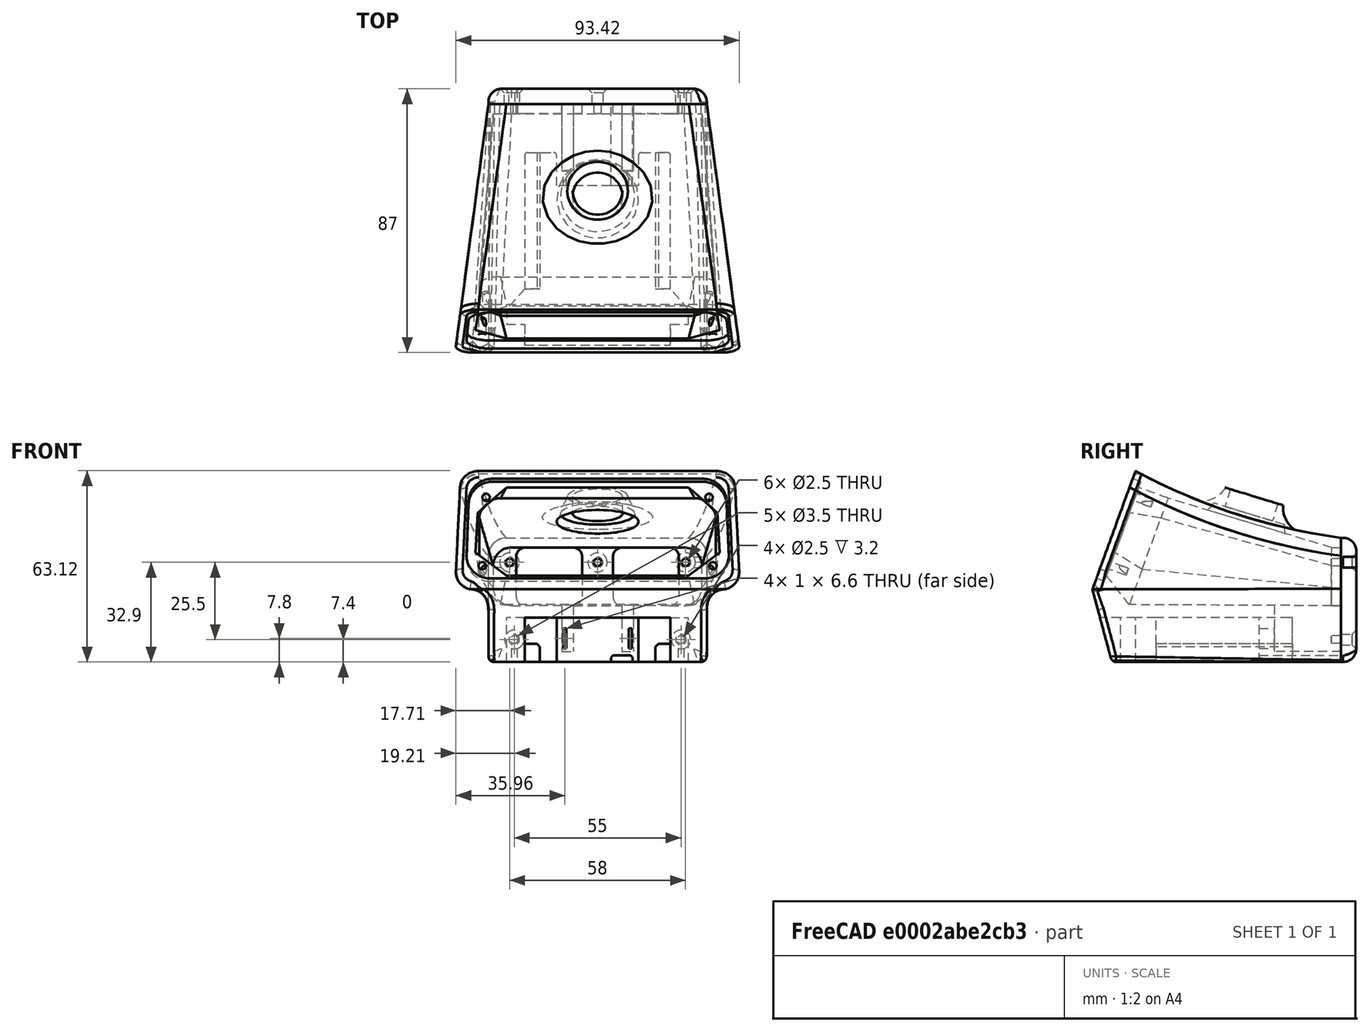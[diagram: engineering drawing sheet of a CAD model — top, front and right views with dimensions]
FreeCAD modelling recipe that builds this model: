
FCSTD DOCUMENT  (FreeCAD 0.19R24267 (Git))
Label: solder_station3
License: All rights reserved
LicenseURL: http://en.wikipedia.org/wiki/All_rights_reserved
objects: Sketcher::SketchObject×17, PartDesign::Pocket×7, Mesh::Feature×3, PartDesign::Pad×3, PartDesign::SubtractiveLoft×2, PartDesign::Fillet×2, PartDesign::Body×2, Spreadsheet::Sheet×1, PartDesign::Revolution×1, PartDesign::Groove×1, PartDesign::Chamfer×1, App::Part×1, Part::Fillet×1, App::DocumentObjectGroup×1
note: 54 computed .brp shape members not serialized (recipe doc carries the construction recipe); baked Part::Feature solids carry a one-line shape summary decoded from their .brp

FEATURE [Sketcher::SketchObject] Sketch  label="RearSupport"
  AttachmentOffset = pos=(0,0,-37.8) rot=(0,0,1;0rad)
  FullyConstrained = true
  MapMode = 5
  Placement = pos=(0,37.8,8.4e-15) rot=(1,0,0;1.5708rad)
  Support = -> [XZ_Plane004]
  expr: Constraints[51] = <<param>>.rear_screw_height
  expr: Constraints[50] = <<param>>.rear_screw_height
  expr: Constraints[49] = <<param>>.screw_hole
  expr: Constraints[52] = <<param>>.rear_screw_offset
  expr: Constraints[48] = <<param>>.rear_screw_width1
  expr: Constraints[47] = <<param>>.reart_screw_width2
  expr: Constraints[24] = 3
  expr: Constraints[39] = <<param>>.rear_height - <<param>>.wall
  expr: Constraints[38] = <<param>>.floor
  expr: Constraints[37] = <<param>>.bottom_height
  expr: .AttachmentOffset.Base.z = -<<param>>.mid_depth / 2 + <<param>>.wall
  sketch-geometry (22):
    g0: LineSegment StartX=-23.8 StartY=13.8 StartZ=0 EndX=-8.1 EndY=13.8 EndZ=0
    g1: LineSegment StartX=26.8 StartY=10.8 StartZ=0 EndX=26.8 EndY=-2.4 EndZ=0
    g2: LineSegment StartX=23.8 StartY=-5.4 StartZ=0 EndX=8.1 EndY=-5.4 EndZ=0
    g3: LineSegment StartX=-26.8 StartY=-2.4 StartZ=0 EndX=-26.8 EndY=10.8 EndZ=0
    g4: LineSegment StartX=-5.1 StartY=10.8 StartZ=0 EndX=-5.1 EndY=-2.4 EndZ=0
    g5: LineSegment StartX=5.1 StartY=10.8 StartZ=0 EndX=5.1 EndY=-2.4 EndZ=0
    g6: LineSegment StartX=8.1 StartY=13.8 StartZ=0 EndX=23.8 EndY=13.8 EndZ=0
    g7: LineSegment StartX=-8.1 StartY=-5.4 StartZ=0 EndX=-23.8 EndY=-5.4 EndZ=0
    g8: ArcOfCircle CenterX=-8.1 CenterY=10.8 CenterZ=0 NormalX=0 NormalY=0 NormalZ=1 AngleXU=0 Radius=3 StartAngle=0 EndAngle=1.5708
    g9: ArcOfCircle CenterX=8.1 CenterY=10.8 CenterZ=0 NormalX=0 NormalY=0 NormalZ=1 AngleXU=0 Radius=3 StartAngle=1.5708 EndAngle=3.14159
    g10: ArcOfCircle CenterX=-8.1 CenterY=-2.4 CenterZ=0 NormalX=0 NormalY=0 NormalZ=1 AngleXU=0 Radius=3 StartAngle=4.71239 EndAngle=6.28319
    g11: ArcOfCircle CenterX=8.1 CenterY=-2.4 CenterZ=0 NormalX=0 NormalY=0 NormalZ=1 AngleXU=0 Radius=3 StartAngle=3.14159 EndAngle=4.71239
    g12: ArcOfCircle CenterX=-23.8 CenterY=10.8 CenterZ=0 NormalX=0 NormalY=0 NormalZ=1 AngleXU=0 Radius=3 StartAngle=1.5708 EndAngle=3.14159
    g13: ArcOfCircle CenterX=-23.8 CenterY=-2.4 CenterZ=0 NormalX=0 NormalY=0 NormalZ=1 AngleXU=0 Radius=3 StartAngle=3.14159 EndAngle=4.71239
    g14: ArcOfCircle CenterX=23.8 CenterY=10.8 CenterZ=0 NormalX=0 NormalY=0 NormalZ=1 AngleXU=0 Radius=3 StartAngle=0 EndAngle=1.5708
    g15: ArcOfCircle CenterX=23.8 CenterY=-2.4 CenterZ=0 NormalX=0 NormalY=0 NormalZ=1 AngleXU=0 Radius=3 StartAngle=4.71239 EndAngle=6.28319
    g16: Circle CenterX=0 CenterY=-24 CenterZ=0 NormalX=0 NormalY=0 NormalZ=1 AngleXU=0 Radius=3
    g17: Circle CenterX=0 CenterY=8.9 CenterZ=0 NormalX=0 NormalY=0 NormalZ=1 AngleXU=0 Radius=1.25
    g18: Circle CenterX=-29 CenterY=8.9 CenterZ=0 NormalX=0 NormalY=0 NormalZ=1 AngleXU=0 Radius=1.25
    g19: Circle CenterX=-27.5 CenterY=-16.6 CenterZ=0 NormalX=0 NormalY=0 NormalZ=1 AngleXU=0 Radius=1.25
    g20: Circle CenterX=27.5 CenterY=-16.6 CenterZ=0 NormalX=0 NormalY=0 NormalZ=1 AngleXU=0 Radius=1.25
    g21: Circle CenterX=29 CenterY=8.9 CenterZ=0 NormalX=0 NormalY=0 NormalZ=1 AngleXU=0 Radius=1.25
  constraints (53):
    c: Horizontal(g0)
    c: Horizontal(g2)
    c: Vertical(g1)
    c: Vertical(g3)
    c: Vertical(g4)
    c: Vertical(g5)
    c: Tangent(g0,g6)
    c: Tangent(g2,g7)
    c: Tangent(g0,g8) = 1.5708
    c: Tangent(g4,g8) = 1.5708
    c: Tangent(g5,g9) = -1.5708
    c: Tangent(g6,g9) = 1.5708
    c: Tangent(g7,g10) = 1.5708
    c: Tangent(g4,g10) = 1.5708
    c: Tangent(g5,g11) = -1.5708
    c: Tangent(g2,g11) = 1.5708
    c: Tangent(g0,g12) = 1.5708
    c: Tangent(g3,g12) = 1.5708
    c: Tangent(g3,g13) = 1.5708
    c: Tangent(g7,g13) = 1.5708
    c: Tangent(g6,g14) = 1.5708
    c: Tangent(g1,g14) = 1.5708
    c: Tangent(g1,g15) = 1.5708
    c: Tangent(g2,g15) = 1.5708
    c: Radius(g9) = 3
    c: Equal(g12,g13)
    c: Equal(g13,g10)
    c: Equal(g10,g8)
    c: Equal(g11,g15)
    c: Equal(g15,g14)
    c: Equal(g14,g9)
    c: DistanceX(g4,g-1) = 5.1
    c: DistanceX(g5,g1) = 21.7
    c: Symmetric(g4,g5,g-2)
    c: Equal(g7,g2)
    c: PointOnObject(g16,g-2)
    c: Radius(g16) = 3
    c: DistanceY(g16,g-1) = 24
    c: DistanceY(g16,g2) = 18.6
    c: DistanceY(g16,g6) = 37.8
    c: PointOnObject(g17,g-2)
    c: Equal(g21,g18)
    c: Equal(g18,g19)
    c: Equal(g19,g20)
    c: Equal(g18,g17)
    c: Symmetric(g20,g19,g-2)
    c: Symmetric(g18,g21,g-2)
    c: DistanceX(g19,g20) = 55
    c: DistanceX(g18,g21) = 58
    c: Diameter(g19) = 2.5
    c: DistanceY(g20,g21) = 25.5
    c: DistanceY(g20,g17) = 25.5
    c: DistanceY(g16,g19) = 7.4
FEATURE [Spreadsheet::Sheet] Spreadsheet  label="param"
  cells = A1=Body; B2=top_depth; C2(top_depth)=70; B3=mid_depth; C3(mid_depth)=82; D3=half is rear reference; B4=bottom_depth; C4(bottom_depth)=75; B6=bottom_width; C6(bottom_width)=72; B7=bottom_height; C7(bottom_height)=24; B8=bottom_angle; C8(bottom_angle)=15; B10=rear_width; C10(rear_width)=72; B11=rear_height; C11(rear_height)=41; B13=mid_width; C13(mid_width)=80; B14=mid_height; C14(mid_height)=50; B16=front_width1; C16(front_width1)=91; D16=@top; E16=upper; B17=front_width2; C17(front_width2)=94; D17=@mid; E17=lower; B18=front_height; C18(front_height)=63; B19=front_angle; C19(front_angle)=20; B21=wall; C21(wall)=3.2; B22=radius_big; C22(radius_big)=6; B23=radius_small; C23(radius_small)=2; B24=arch; C24(arch)=200; A26=Button; B27=button_offset; C27(button_offset)=10; B28=button_inside_dia; C28(button_inside_dia)=20; B29=button_outside_dia; C29(button_outside_dia)=50; B30=button_height; C30(button_height)=23; B31=button_extension; C31(button_extension)=8; B32=button_fillet; C32(button_fillet)=12; B33=button_angle; C33(button_angle)=-17; B34=button_hole; C34(button_hole)=16.4; B35=button_hole_center; C35(button_hole_center)=-0.5; A37=Battery Cuts; B38=batt_carveout; C38(batt_carveout)=14.6; B39=batt_rail; C39(batt_rail)=6; B40=batt_rail_length; C40(batt_rail_length)=45; A42=Terminals; B43=terminal_height; C43(terminal_height)=6.6; B44=terminal_thickness; C44(terminal_thickness)=1; B45=terminal_seperation; C45(terminal_seperation)=21.5; B46=terminal_offset; C46(terminal_offset)=4.5; B47=terminal_depth; C47(terminal_depth)=22; A49=Box Interior; B50=floor; C50(floor)=18.6; B51=rear_inside_width; C51(rear_inside_width)==C10 - C21; D51=calc; B52=rear_inside_height; C52(rear_inside_height)==C11 - C21; D52=calc; B53=mid_inside_width; C53(mid_inside_width)==C13; D53=calc; B54=mid_inside_height; C54(mid_inside_height)==C14 + 6; D54=calc; B55=front_inside_width1; C55(front_inside_width1)==C62 - C58 * 2; D55=calc; E55=upper; B56=front_inside_width2; C56(front_inside_width2)==C63 - C58 * 2; D56=calc; E56=lower; B57=front_inside_height; C57(front_inside_height)==C64 - C59 * 2; D57=calc; B58=front_width_lip_width; C58(front_width_lip_width)=3; B59=front_inside_lip_height; C59(front_inside_lip_height)=2; A61=Face; B62=face_width1; C62(face_width1)==84 + 1; B63=face_width2; C63(face_width2)==85.5 + 1; B64=face_height; C64(face_height)==34 + 1; B65=face_thickness; C65(face_thickness)=3; B66=face_radius; C66(face_radius)=8; B67=face_offset; C67(face_offset)=2.8; D67=2.8; A69=Screws; B70=screw_hole; C70(screw_hole)=2.5; B72=front_screw_width1; C72(front_screw_width1)=73.5; D72=upper; B73=front_screw_width2; C73(front_screw_width2)=76; D73=lower; B74=front_screw_height; C74(front_screw_height)=24; B75=front_screw_offset; C75(front_screw_offset)=5.5; B77=rear_screw_width1; C77(rear_screw_width1)=58; B78=reart_screw_width2; C78(reart_screw_width2)=55; B79=rear_screw_height; C79(rear_screw_height)=25.5; B80=rear_screw_offset; C80(rear_screw_offset)=7.4
FEATURE [Sketcher::SketchObject] Sketch008  label="SketchButtonHole"
  AttachmentOffset = pos=(0,-0.5,23) rot=(1,0,0;-0.296706rad)
  FullyConstrained = true
  MapMode = 5
  Placement = pos=(0,-0.5,23) rot=(1,0,0;5.98648rad)
  Support = -> [XY_Plane004]
  expr: Constraints[2] = <<param>>.button_offset
  expr: .AttachmentOffset.Rotation.Angle = <<param>>.button_angle
  expr: .AttachmentOffset.Base.y = <<param>>.button_hole_center
  expr: Constraints[0] = <<param>>.button_hole
  expr: .AttachmentOffset.Base.z = <<param>>.button_height
  sketch-geometry (1):
    g0: Circle CenterX=0 CenterY=10 CenterZ=0 NormalX=0 NormalY=0 NormalZ=1 AngleXU=0 Radius=8.2
  constraints (3):
    c: Diameter(g0) = 16.4
    c: PointOnObject(g0,g-2)
    c: DistanceY(g-1,g0) = 10
FEATURE [Mesh::Feature] M18_soldering_case
  Placement = pos=(48,-41,-24) rot=(0,0.707107,0.707107;3.14159rad)
FEATURE [Sketcher::SketchObject] Sketch012  label="SketchSide"
  FullyConstrained = true
  MapMode = 5
  Placement = pos=(0,0,0) rot=(0.57735,0.57735,0.57735;2.0944rad)
  Support = -> [YZ_Plane004]
  expr: Constraints[21] = <<param>>.front_height
  expr: Constraints[6] = <<param>>.mid_depth
  expr: Constraints[17] = 90 - <<param>>.front_angle
  expr: Constraints[14] = <<param>>.bottom_height
  expr: Constraints[4] = <<param>>.rear_height - <<param>>.bottom_height
  expr: Constraints[5] = <<param>>.arch
  expr: Constraints[15] = <<param>>.radius_small
  expr: Constraints[16] = 90 - <<param>>.bottom_angle
  sketch-geometry (7):
    g0: LineSegment StartX=41 StartY=0 StartZ=0 EndX=41 EndY=17 EndZ=0
    g1: LineSegment StartX=-41 StartY=0 StartZ=0 EndX=-26.8052 EndY=39 EndZ=0
    g2: ArcOfCircle CenterX=67.8335 CenterY=215.192 CenterZ=0 NormalX=0 NormalY=0 NormalZ=1 AngleXU=0 Radius=200 StartAngle=4.21948 EndAngle=4.57782
    g3: LineSegment StartX=-41 StartY=0 StartZ=0 EndX=-34.9664 EndY=-22.5176 EndZ=0
    g4: LineSegment StartX=-33.0346 StartY=-24 StartZ=0 EndX=41 EndY=-24 EndZ=0
    g5: LineSegment StartX=41 StartY=-24 StartZ=0 EndX=41 EndY=0 EndZ=0
    g6: ArcOfCircle CenterX=-33.0346 CenterY=-22 CenterZ=0 NormalX=0 NormalY=0 NormalZ=1 AngleXU=0 Radius=2 StartAngle=3.40339 EndAngle=4.71239
  constraints (22):
    c: PointOnObject(g1,g-1)
    c: Vertical(g0)
    c: Coincident(g2,g0)
    c: Symmetric(g1,g0,g-2)
    c: DistanceY(g0,g0) = 17
    c: Radius(g2) = 200
    c: DistanceX(g1,g0) = 82
    c: Horizontal(g4)
    c: Coincident(g5,g4)
    c: Vertical(g5)
    c: Coincident(g6,g3)
    c: Coincident(g6,g4)
    c: Tangent(g6,g4)
    c: Tangent(g6,g3)
    c: DistanceY(g4,g-1) = 24
    c: Radius(g6) = 2
    c: Angle(g3,g-1) = 1.309
    c: Angle(g-1,g1) = 1.22173
    c: Coincident(g3,g1)
    c: Coincident(g5,g0)
    c: Coincident(g2,g1)
    c: DistanceY(g4,g1) = 63
FEATURE [Sketcher::SketchObject] Sketch018  label="SketchBat1"
  AttachmentOffset = pos=(0,0,-24) rot=(0,0,1;0rad)
  FullyConstrained = true
  MapMode = 5
  Placement = pos=(0,0,-24) rot=(0,0,1;0rad)
  Support = -> [XY_Plane004]
  expr: Constraints[64] = <<param>>.mid_depth / 2
  expr: .AttachmentOffset.Base.z = -<<param>>.bottom_height
  expr: Constraints[63] = <<param>>.batt_rail_length
  sketch-geometry (21):
    g0: LineSegment StartX=-24 StartY=-41.7082 StartZ=0 EndX=24 EndY=-41.7082 EndZ=0
    g1: LineSegment StartX=24 StartY=-41.7082 StartZ=0 EndX=24 EndY=-31.7082 EndZ=0
    g2: LineSegment StartX=24 StartY=-31.7082 StartZ=0 EndX=30 EndY=-31.7082 EndZ=0
    g3: LineSegment StartX=30 StartY=-31.7082 StartZ=0 EndX=30 EndY=-26.7082 EndZ=0
    g4: LineSegment StartX=30 StartY=-26.7082 StartZ=0 EndX=24 EndY=-20 EndZ=0
    g5: LineSegment StartX=24 StartY=-20 StartZ=0 EndX=24 EndY=24 EndZ=0
    g6: LineSegment StartX=13.5 StartY=24 StartZ=0 EndX=13.5 EndY=14 EndZ=0
    g7: LineSegment StartX=13.5 StartY=14 StartZ=0 EndX=-13.5 EndY=14 EndZ=0
    g8: LineSegment StartX=-13.5 StartY=14 StartZ=0 EndX=-13.5 EndY=24 EndZ=0
    g9: LineSegment StartX=-24 StartY=24 StartZ=0 EndX=-24 EndY=-20 EndZ=0
    g10: LineSegment StartX=-24 StartY=-20 StartZ=0 EndX=-30 EndY=-26.7082 EndZ=0
    g11: LineSegment StartX=-30 StartY=-26.7082 StartZ=0 EndX=-30 EndY=-31.7082 EndZ=0
    g12: LineSegment StartX=-30 StartY=-31.7082 StartZ=0 EndX=-24 EndY=-31.7082 EndZ=0
    g13: LineSegment StartX=-24 StartY=-31.7082 StartZ=0 EndX=-24 EndY=-41.7082 EndZ=0
    g14: Circle CenterX=0 CenterY=41 CenterZ=0 NormalX=0 NormalY=0 NormalZ=1 AngleXU=0 Radius=4
    g15: ArcOfCircle CenterX=-14.5 CenterY=24 CenterZ=0 NormalX=0 NormalY=0 NormalZ=1 AngleXU=0 Radius=1 StartAngle=6.28318 EndAngle=7.85399
    g16: LineSegment StartX=-23 StartY=25 StartZ=0 EndX=-14.5 EndY=25 EndZ=0
    g17: LineSegment StartX=14.5 StartY=25 StartZ=0 EndX=23 EndY=25 EndZ=0
    g18: ArcOfCircle CenterX=-23 CenterY=24 CenterZ=0 NormalX=0 NormalY=0 NormalZ=1 AngleXU=0 Radius=1 StartAngle=1.5708 EndAngle=3.1416
    g19: ArcOfCircle CenterX=14.5 CenterY=24 CenterZ=0 NormalX=0 NormalY=0 NormalZ=1 AngleXU=0 Radius=1 StartAngle=1.5708 EndAngle=3.14159
    g20: ArcOfCircle CenterX=23 CenterY=24 CenterZ=0 NormalX=0 NormalY=0 NormalZ=1 AngleXU=0 Radius=1.00001 StartAngle=2.74851e-06 EndAngle=1.5708
  constraints (65):
    c: Horizontal(g0)
    c: Coincident(g1,g0)
    c: Vertical(g1)
    c: Coincident(g2,g1)
    c: Horizontal(g2)
    c: Coincident(g3,g2)
    c: Coincident(g3,g4)
    c: Vertical(g5)
    c: Coincident(g6,g7)
    c: Coincident(g7,g8)
    c: Vertical(g8)
    c: Vertical(g9)
    c: Coincident(g10,g11)
    c: Vertical(g11)
    c: Coincident(g11,g12)
    c: Horizontal(g12)
    c: Coincident(g12,g13)
    c: Equal(g6,g8)
    c: Equal(g5,g9)
    c: Equal(g4,g10)
    c: Equal(g3,g11)
    c: Equal(g12,g2)
    c: Equal(g1,g13)
    c: Coincident(g13,g0)
    c: Vertical(g13)
    c: DistanceX(g7,g7) = 27
    c: Symmetric(g7,g6,g-2)
    c: Distance(g4) = 9
    c: Vertical(g3)
    c: DistanceY(g3,g3) = 5
    c: DistanceX(g2,g2) = 6
    c: DistanceY(g1,g1) = 10
    c: DistanceX(g0,g0) = 48
    c: PointOnObject(g14,g-2)
    c: Coincident(g9,g10)
    c: Coincident(g5,g4)
    c: Coincident(g15,g8)
    c: Coincident(g16,g15)
    c: Tangent(g15,g8)
    c: Horizontal(g16)
    c: Horizontal(g17)
    c: DistanceX(g9,g5) = 48
    c: Symmetric(g4,g9,g-2)
    c: Equal(g16,g17)
    c: Coincident(g18,g9)
    c: Coincident(g18,g16)
    c: Equal(g18,g15)
    c: Tangent(g18,g16)
    c: Tangent(g18,g9)
    c: DistanceY(g6,g17) = 11
    c: Vertical(g6)
    c: Coincident(g19,g6)
    c: Coincident(g19,g17)
    c: Coincident(g20,g17)
    c: Coincident(g20,g5)
    c: Tangent(g20,g17)
    c: Tangent(g20,g5)
    c: Tangent(g19,g6)
    c: Tangent(g19,g17)
    c: Equal(g15,g19)
    c: Radius(g19) = 1
    c: Radius(g14) = 4
    c: DistanceY(g15,g14) = 16
    c: DistanceY(g9,g16) = 45
    c: DistanceY(g-1,g14) = 41
FEATURE [Sketcher::SketchObject] Sketch019  label="SketchBat2"
  AttachmentOffset = pos=(0,0,-25) rot=(0,0,1;0rad)
  FullyConstrained = true
  MapMode = 5
  Placement = pos=(0,25,5.6e-15) rot=(1,0,0;1.5708rad)
  Support = -> [XZ_Plane004]
  expr: Constraints[18] = <<param>>.batt_rail
  expr: Constraints[17] = <<param>>.bottom_height
  expr: .AttachmentOffset.Base.z = -<<param>>.mid_depth / 2 + 16
  expr: Constraints[19] = 48.01mm
  sketch-geometry (10):
    g0: LineSegment StartX=-24.005 StartY=-18 StartZ=0 EndX=-20.005 EndY=-18 EndZ=0
    g1: LineSegment StartX=-19.005 StartY=-24 StartZ=0 EndX=-24.005 EndY=-24 EndZ=0
    g2: LineSegment StartX=-24.005 StartY=-24 StartZ=0 EndX=-24.005 EndY=-18 EndZ=0
    g3: LineSegment StartX=24.005 StartY=-18 StartZ=0 EndX=20.005 EndY=-18 EndZ=0
    g4: LineSegment StartX=19.005 StartY=-24 StartZ=0 EndX=24.005 EndY=-24 EndZ=0
    g5: LineSegment StartX=24.005 StartY=-24 StartZ=0 EndX=24.005 EndY=-18 EndZ=0
    g6: LineSegment StartX=-19.005 StartY=-19 StartZ=0 EndX=-19.005 EndY=-24 EndZ=0
    g7: LineSegment StartX=19.005 StartY=-24 StartZ=0 EndX=19.005 EndY=-19 EndZ=0
    g8: LineSegment StartX=-20.005 StartY=-18 StartZ=0 EndX=-19.005 EndY=-19 EndZ=0
    g9: LineSegment StartX=19.005 StartY=-19 StartZ=0 EndX=20.005 EndY=-18 EndZ=0
  constraints (29):
    c: Coincident(g1,g2)
    c: Coincident(g2,g0)
    c: Horizontal(g0)
    c: Horizontal(g1)
    c: Vertical(g2)
    c: Coincident(g4,g5)
    c: Coincident(g5,g3)
    c: Horizontal(g3)
    c: Horizontal(g4)
    c: Vertical(g5)
    c: Coincident(g6,g1)
    c: Vertical(g6)
    c: Equal(g1,g4)
    c: Coincident(g7,g4)
    c: Vertical(g7)
    c: Equal(g6,g7)
    c: Symmetric(g1,g4,g-2)
    c: DistanceY(g1,g-1) = 24
    c: DistanceY(g4,g3) = 6
    c: DistanceX(g1,g4) = 48.01
    c: DistanceX(g4,g4) = 5
    c: Coincident(g8,g0)
    c: Coincident(g8,g6)
    c: Coincident(g9,g7)
    c: Coincident(g9,g3)
    c: Equal(g0,g3)
    c: Equal(g2,g5)
    c: DistanceX(g0,g0) = 4
    c: DistanceY(g1,g6) = 5
FEATURE [Sketcher::SketchObject] Sketch021  label="SketchButton"
  AttachmentOffset = pos=(10,23,0) rot=(0,0,1;-0.296706rad)
  FullyConstrained = false
  MapMode = 5
  Placement = pos=(-2.9e-15,10,23) rot=(-0.51122,-0.690875,-0.51122;4.35074rad)
  Support = -> [YZ_Plane004]
  expr: Constraints[6] = <<param>>.button_extension
  expr: Constraints[7] = <<param>>.button_inside_dia / 2
  expr: Constraints[8] = <<param>>.button_outside_dia / 2
  expr: .AttachmentOffset.Base.y = <<param>>.button_height
  expr: .AttachmentOffset.Rotation.Angle = <<param>>.button_angle
  expr: .AttachmentOffset.Base.x = <<param>>.button_offset
  sketch-geometry (9):
    g0: LineSegment StartX=0 StartY=0 StartZ=0 EndX=0 EndY=8 EndZ=0
    g1: LineSegment StartX=0 StartY=8 StartZ=0 EndX=10 EndY=8 EndZ=0
    g2: LineSegment StartX=0 StartY=0 StartZ=0 EndX=25 EndY=0 EndZ=0
    g3: Circle CenterX=10 CenterY=8 CenterZ=0 NormalX=0 NormalY=0 NormalZ=1 AngleXU=0 Radius=1
    g4: Circle CenterX=11.7708 CenterY=0 CenterZ=0 NormalX=0 NormalY=0 NormalZ=1 AngleXU=0 Radius=1
    g5: Circle CenterX=25 CenterY=0 CenterZ=0 NormalX=0 NormalY=0 NormalZ=1 AngleXU=0 Radius=1
    g6: BSplineCurve PolesCount=3 KnotsCount=2 Degree=2 IsPeriodic=0
    g7: GeomPoint X=10 Y=8 Z=0
    g8: GeomPoint X=25 Y=0 Z=0
  constraints (20):
    c: Coincident(g0,g-1)
    c: PointOnObject(g0,g-2)
    c: Coincident(g1,g0)
    c: Horizontal(g1)
    c: Coincident(g2,g0)
    c: Horizontal(g2)
    c: DistanceY(g0,g0) = 8
    c: DistanceX(g1,g1) = 10
    c: DistanceX(g2,g2) = 25
    c: Coincident(g6,g1)
    c: Weight(g3) = 1
    c: Equal(g3,g4)
    c: Equal(g3,g5)
    c: Coincident(g6,g2)
    c: InternalAlignment(g3,g6)
    c: InternalAlignment(g4,g6)
    c: InternalAlignment(g5,g6)
    c: InternalAlignment(g7,g6)
    c: InternalAlignment(g8,g6)
    c: PointOnObject(g4,g2)
FEATURE [Sketcher::SketchObject] Sketch022  label="SketchRearInside"
  AttachmentOffset = pos=(0,0,-37.8) rot=(0,0,1;0rad)
  FullyConstrained = true
  MapMode = 5
  Placement = pos=(0,37.8,8.4e-15) rot=(1,0,0;1.5708rad)
  Support = -> [XZ_Plane004]
  expr: Constraints[29] = <<param>>.floor
  expr: Constraints[26] = <<param>>.bottom_height
  expr: Constraints[27] = <<param>>.rear_inside_height
  expr: .AttachmentOffset.Base.z = -<<param>>.mid_depth / 2 + <<param>>.wall
  expr: Constraints[18] = <<param>>.rear_inside_width
  expr: Constraints[12] = <<param>>.radius_big
  sketch-geometry (9):
    g0: LineSegment StartX=-34.4 StartY=7.80002 StartZ=0 EndX=-34.4 EndY=0.600003 EndZ=0
    g1: LineSegment StartX=-28.4 StartY=-5.4 StartZ=0 EndX=28.4 EndY=-5.4 EndZ=0
    g2: LineSegment StartX=34.4 StartY=0.600003 StartZ=0 EndX=34.4 EndY=7.80002 EndZ=0
    g3: LineSegment StartX=-28.4 StartY=13.8 StartZ=0 EndX=28.4 EndY=13.8 EndZ=0
    g4: ArcOfCircle CenterX=28.4 CenterY=7.8 CenterZ=0 NormalX=0 NormalY=0 NormalZ=1 AngleXU=0 Radius=6 StartAngle=3.92565e-06 EndAngle=1.5708
    g5: ArcOfCircle CenterX=28.4 CenterY=0.6 CenterZ=0 NormalX=0 NormalY=0 NormalZ=1 AngleXU=0 Radius=6 StartAngle=4.71239 EndAngle=6.28319
    g6: ArcOfCircle CenterX=-28.4 CenterY=7.8 CenterZ=0 NormalX=0 NormalY=0 NormalZ=1 AngleXU=0 Radius=6 StartAngle=1.5708 EndAngle=3.14159
    g7: ArcOfCircle CenterX=-28.4 CenterY=0.6 CenterZ=0 NormalX=0 NormalY=0 NormalZ=1 AngleXU=0 Radius=6 StartAngle=3.14159 EndAngle=4.71239
    g8: Circle CenterX=0 CenterY=-24 CenterZ=0 NormalX=0 NormalY=0 NormalZ=1 AngleXU=0 Radius=3
  constraints (30):
    c: Vertical(g0)
    c: Horizontal(g1)
    c: Vertical(g2)
    c: Horizontal(g3)
    c: Equal(g3,g1)
    c: Equal(g0,g2)
    c: Coincident(g4,g3)
    c: Coincident(g4,g2)
    c: Coincident(g5,g2)
    c: Coincident(g5,g1)
    c: Coincident(g6,g0)
    c: Coincident(g6,g3)
    c: Radius(g6) = 6
    c: Equal(g6,g4)
    c: Equal(g4,g5)
    c: Coincident(g7,g1)
    c: Coincident(g7,g0)
    c: Equal(g5,g7)
    c: DistanceX(g0,g2) = 68.8
    c: Symmetric(g0,g2,g-2)
    c: Tangent(g4,g2)
    c: Tangent(g4,g3)
    c: Tangent(g5,g2)
    c: Tangent(g5,g1)
    c: Tangent(g6,g3)
    c: PointOnObject(g8,g-2)
    c: DistanceY(g8,g-1) = 24
    c: DistanceY(g8,g3) = 37.8
    c: Radius(g8) = 3
    c: DistanceY(g8,g1) = 18.6
FEATURE [Sketcher::SketchObject] Sketch023  label="SketchFrontInside"
  AttachmentOffset = pos=(0,0,38) rot=(1,0,0;-0.349066rad)
  FullyConstrained = true
  MapMode = 5
  Placement = pos=(0,-38,-8.4e-15) rot=(-1,0,0;5.06145rad)
  Support = -> [XZ_Plane004]
  expr: Constraints[19] = <<param>>.front_inside_width2
  expr: Constraints[20] = <<param>>.front_inside_width2 / 2
  expr: Constraints[21] = <<param>>.face_offset + <<param>>.front_inside_lip_height
  expr: .AttachmentOffset.Rotation.Angle = -<<param>>.front_angle
  expr: Constraints[2] = <<param>>.front_inside_height
  expr: .AttachmentOffset.Base.z = <<param>>.mid_depth / 2 - <<param>>.face_thickness
  expr: Constraints[1] = <<param>>.front_inside_width1
  sketch-geometry (8):
    g0: LineSegment StartX=-30 StartY=4.8 StartZ=0 EndX=30 EndY=4.8 EndZ=0
    g1: LineSegment StartX=30 StartY=35.8 StartZ=0 EndX=-30 EndY=35.8 EndZ=0
    g2: LineSegment StartX=-39.5 StartY=26.8643 StartZ=0 EndX=-40.25 EndY=12.8643 EndZ=0
    g3: LineSegment StartX=-39.5 StartY=26.8643 StartZ=0 EndX=-30 EndY=35.8 EndZ=0
    g4: LineSegment StartX=30 StartY=35.8 StartZ=0 EndX=39.5 EndY=26.8643 EndZ=0
    g5: LineSegment StartX=40.25 StartY=12.8643 StartZ=0 EndX=30 EndY=4.8 EndZ=0
    g6: LineSegment StartX=-40.25 StartY=12.8643 StartZ=0 EndX=-30 EndY=4.8 EndZ=0
    g7: LineSegment StartX=39.5 StartY=26.8643 StartZ=0 EndX=40.25 EndY=12.8643 EndZ=0
  constraints (22):
    c: Symmetric(g0,g0,g-2)
    c: DistanceX(g2,g4) = 79
    c: DistanceY(g0,g1) = 31
    c: Symmetric(g1,g1,g-2)
    c: Coincident(g3,g2)
    c: Coincident(g3,g1)
    c: Coincident(g4,g1)
    c: Coincident(g5,g0)
    c: Coincident(g6,g2)
    c: Coincident(g6,g0)
    c: Equal(g3,g6)
    c: Equal(g6,g5)
    c: Equal(g5,g4)
    c: Coincident(g7,g4)
    c: Coincident(g7,g5)
    c: DistanceY(g7,g7) = 14
    c: Equal(g7,g2)
    c: Equal(g1,g0)
    c: DistanceX(g1,g1) = 60
    c: DistanceX(g2,g5) = 80.5
    c: DistanceX(g2,g-1) = 40.25
    c: DistanceY(g-1,g0) = 4.8
FEATURE [Sketcher::SketchObject] Sketch024  label="SketchFace"
  AttachmentOffset = pos=(0,0,38) rot=(1,0,0;-0.349066rad)
  FullyConstrained = true
  MapMode = 5
  Placement = pos=(0,-38,-8.4e-15) rot=(-1,0,0;5.06145rad)
  Support = -> [XZ_Plane004]
  expr: Constraints[25] = <<param>>.face_height
  expr: Constraints[24] = <<param>>.face_offset
  expr: .AttachmentOffset.Rotation.Angle = -<<param>>.front_angle
  expr: Constraints[22] = <<param>>.face_width1
  expr: Constraints[13] = <<param>>.face_radius
  expr: .AttachmentOffset.Base.z = <<param>>.mid_depth / 2 - <<param>>.face_thickness
  expr: Constraints[23] = <<param>>.face_width2
  sketch-geometry (8):
    g0: LineSegment StartX=-34.5062 StartY=37.8 StartZ=0 EndX=34.5063 EndY=37.8 EndZ=0
    g1: LineSegment StartX=42.5001 StartY=30.1155 StartZ=0 EndX=43.25 EndY=11.1155 EndZ=0
    g2: LineSegment StartX=35.2562 StartY=2.8 StartZ=0 EndX=-35.2562 EndY=2.8 EndZ=0
    g3: LineSegment StartX=-43.25 StartY=11.1156 StartZ=0 EndX=-42.4999 EndY=30.1156 EndZ=0
    g4: ArcOfCircle CenterX=34.5063 CenterY=29.8 CenterZ=0 NormalX=0 NormalY=0 NormalZ=1 AngleXU=0 Radius=8 StartAngle=0.0394514 EndAngle=1.5708
    g5: ArcOfCircle CenterX=35.2563 CenterY=10.8 CenterZ=0 NormalX=0 NormalY=0 NormalZ=1 AngleXU=0 Radius=8 StartAngle=4.71239 EndAngle=6.32264
    g6: ArcOfCircle CenterX=-34.5062 CenterY=29.8 CenterZ=0 NormalX=0 NormalY=0 NormalZ=1 AngleXU=0 Radius=8 StartAngle=1.5708 EndAngle=3.10214
    g7: ArcOfCircle CenterX=-35.2562 CenterY=10.8 CenterZ=0 NormalX=0 NormalY=0 NormalZ=1 AngleXU=0 Radius=8 StartAngle=3.10214 EndAngle=4.71239
  constraints (27):
    c: Horizontal(g0)
    c: Coincident(g4,g0)
    c: Coincident(g4,g1)
    c: Coincident(g5,g1)
    c: Coincident(g5,g2)
    c: Coincident(g6,g0)
    c: Coincident(g6,g3)
    c: Coincident(g7,g3)
    c: Coincident(g7,g2)
    c: Equal(g1,g3)
    c: Equal(g4,g6)
    c: Equal(g6,g7)
    c: Equal(g7,g5)
    c: Radius(g4) = 8
    c: Tangent(g6,g3)
    c: Tangent(g7,g3)
    c: Tangent(g7,g2)
    c: Tangent(g6,g0)
    c: Tangent(g4,g0)
    c: Tangent(g4,g1)
    c: Tangent(g5,g1)
    c: Tangent(g5,g2)
    c: DistanceX(g3,g1) = 85
    c: DistanceX(g3,g1) = 86.5
    c: DistanceY(g-1,g2) = 2.8
    c: DistanceY(g2,g0) = 35
    c: Symmetric(g2,g2,g-2)
FEATURE [Sketcher::SketchObject] Sketch025  label="SketchMidInside"
  AttachmentOffset = pos=(0,0,27) rot=(1,0,0;-0.349066rad)
  FullyConstrained = true
  MapMode = 5
  Placement = pos=(0,-27,-6e-15) rot=(-1,0,0;5.06145rad)
  Support = -> [XZ_Plane004]
  expr: Constraints[4] = <<param>>.bottom_height
  expr: Constraints[10] = <<param>>.radius_big + 1
  expr: Constraints[11] = <<param>>.floor
  expr: .AttachmentOffset.Base.z = <<param>>.mid_depth / 2 - 14
  expr: Constraints[12] = Spreadsheet.mid_inside_width - 2
  expr: Constraints[23] = <<param>>.mid_width - 16
  expr: .AttachmentOffset.Rotation.Angle = -<<param>>.front_angle
  expr: Constraints[14] = <<param>>.mid_inside_height
  sketch-geometry (9):
    g0: LineSegment StartX=-32 StartY=32 StartZ=0 EndX=32 EndY=32 EndZ=0
    g1: LineSegment StartX=39 StartY=25 StartZ=0 EndX=39 EndY=7 EndZ=0
    g2: LineSegment StartX=32 StartY=-5.4 StartZ=0 EndX=-32 EndY=-5.4 EndZ=0
    g3: LineSegment StartX=-39 StartY=7 StartZ=0 EndX=-39 EndY=25 EndZ=0
    g4: Circle CenterX=0 CenterY=-24 CenterZ=0 NormalX=0 NormalY=0 NormalZ=1 AngleXU=0 Radius=3
    g5: ArcOfCircle CenterX=-32 CenterY=25 CenterZ=0 NormalX=0 NormalY=0 NormalZ=1 AngleXU=0 Radius=7 StartAngle=1.5708 EndAngle=3.14159
    g6: ArcOfCircle CenterX=32 CenterY=25 CenterZ=0 NormalX=0 NormalY=0 NormalZ=1 AngleXU=0 Radius=7 StartAngle=0 EndAngle=1.5708
    g7: ArcOfCircle CenterX=-15.541 CenterY=12.0672 CenterZ=0 NormalX=0 NormalY=0 NormalZ=1 AngleXU=0 Radius=24 StartAngle=3.35433 EndAngle=3.9567
    g8: ArcOfCircle CenterX=15.541 CenterY=12.0672 CenterZ=0 NormalX=0 NormalY=0 NormalZ=1 AngleXU=0 Radius=24 StartAngle=5.46808 EndAngle=6.07045
  constraints (25):
    c: Vertical(g1)
    c: Vertical(g3)
    c: PointOnObject(g4,g-2)
    c: Radius(g4) = 3
    c: DistanceY(g4,g-1) = 24
    c: Tangent(g3,g5) = 1.5708
    c: Tangent(g0,g5) = 1.5708
    c: Tangent(g0,g6) = 1.5708
    c: Tangent(g1,g6) = 1.5708
    c: Equal(g6,g5)
    c: Radius(g6) = 7
    c: DistanceY(g4,g2) = 18.6
    c: DistanceX(g3,g1) = 78
    c: Symmetric(g2,g2,g-2)
    c: DistanceY(g4,g0) = 56
    c: Symmetric(g0,g0,g-2)
    c: Equal(g3,g1)
    c: Coincident(g7,g2)
    c: Coincident(g8,g1)
    c: Coincident(g8,g2)
    c: Coincident(g7,g3)
    c: Equal(g8,g7)
    c: Radius(g8) = 24
    c: DistanceX(g2,g2) = 64
    c: DistanceY(g1,g1) = 18
FEATURE [Sketcher::SketchObject] Sketch026  label="SketchFrontScrews"
  AttachmentOffset = pos=(0,0,38) rot=(1,0,0;-0.349066rad)
  FullyConstrained = true
  MapMode = 5
  Placement = pos=(0,-38,-8.4e-15) rot=(-1,0,0;5.06145rad)
  Support = -> [XZ_Plane004]
  expr: .AttachmentOffset.Rotation.Angle = -<<param>>.front_angle
  expr: Constraints[9] = <<param>>.face_offset + <<param>>.front_screw_offset
  expr: .AttachmentOffset.Base.z = <<param>>.mid_depth / 2 - <<param>>.face_thickness
  expr: Constraints[13] = <<param>>.screw_hole
  expr: Constraints[2] = <<param>>.front_screw_height
  expr: Constraints[1] = <<param>>.front_screw_width2
  expr: Constraints[0] = <<param>>.front_screw_width1
  sketch-geometry (6):
    g0: Circle CenterX=-36.75 CenterY=32.3 CenterZ=0 NormalX=0 NormalY=0 NormalZ=1 AngleXU=0 Radius=1.25
    g1: Circle CenterX=36.75 CenterY=32.3 CenterZ=0 NormalX=0 NormalY=0 NormalZ=1 AngleXU=0 Radius=1.25
    g2: Circle CenterX=-38 CenterY=8.3 CenterZ=0 NormalX=0 NormalY=0 NormalZ=1 AngleXU=0 Radius=1.25
    g3: Circle CenterX=38 CenterY=8.3 CenterZ=0 NormalX=0 NormalY=0 NormalZ=1 AngleXU=0 Radius=1.25
    g4: LineSegment StartX=-36.75 StartY=32.3 StartZ=0 EndX=36.75 EndY=32.3 EndZ=0
    g5: LineSegment StartX=-38 StartY=8.3 StartZ=0 EndX=38 EndY=8.3 EndZ=0
  constraints (14):
    c: DistanceX(g0,g1) = 73.5
    c: DistanceX(g2,g3) = 76
    c: DistanceY(g3,g1) = 24
    c: Coincident(g4,g0)
    c: Coincident(g4,g1)
    c: Coincident(g5,g2)
    c: Coincident(g5,g3)
    c: Symmetric(g2,g3,g-2)
    c: Symmetric(g0,g1,g-2)
    c: DistanceY(g-1,g3) = 8.3
    c: Equal(g0,g2)
    c: Equal(g2,g3)
    c: Equal(g3,g1)
    c: Diameter(g0) = 2.5
FEATURE [Sketcher::SketchObject] Sketch027  label="SketchButtonCarve"
  AttachmentOffset = pos=(10,23,0) rot=(0,0,1;-0.296706rad)
  FullyConstrained = true
  MapMode = 5
  Placement = pos=(-2.9e-15,10,23) rot=(-0.51122,-0.690875,-0.51122;4.35074rad)
  Support = -> [YZ_Plane004]
  expr: Constraints[12] = <<param>>.button_hole / 2 + 10
  expr: .AttachmentOffset.Base.x = <<param>>.button_offset
  expr: Constraints[6] = <<param>>.button_hole / 2 + 4
  expr: .AttachmentOffset.Base.y = <<param>>.button_height
  expr: .AttachmentOffset.Rotation.Angle = <<param>>.button_angle
  sketch-geometry (4):
    g0: LineSegment StartX=0 StartY=2 StartZ=0 EndX=12.2 EndY=2 EndZ=0
    g1: ArcOfCircle CenterX=18.2 CenterY=3.09999 CenterZ=0 NormalX=0 NormalY=0 NormalZ=1 AngleXU=0 Radius=6.09999 StartAngle=3.32291 EndAngle=4.71239
    g2: LineSegment StartX=0 StartY=2 StartZ=0 EndX=0 EndY=-3 EndZ=0
    g3: LineSegment StartX=18.2 StartY=-3 StartZ=0 EndX=0 EndY=-3 EndZ=0
  constraints (13):
    c: Horizontal(g0)
    c: Coincident(g1,g0)
    c: Coincident(g2,g0)
    c: Coincident(g3,g1)
    c: Horizontal(g3)
    c: Tangent(g3,g1)
    c: DistanceX(g0,g0) = 12.2
    c: DistanceY(g2,g2) = 5
    c: Coincident(g2,g3)
    c: Vertical(g2)
    c: PointOnObject(g-1,g2)
    c: DistanceY(g2,g-1) = 3
    c: DistanceX(g3,g3) = 18.2
FEATURE [Sketcher::SketchObject] Sketch028  label="SketchTerminals"
  FullyConstrained = true
  MapMode = 5
  Placement = pos=(0,0,0) rot=(1,0,0;1.5708rad)
  Support = -> [XZ_Plane004]
  expr: Constraints[24] = <<param>>.terminal_seperation
  expr: Constraints[23] = <<param>>.terminal_offset
  expr: Constraints[19] = <<param>>.terminal_height
  expr: Constraints[22] = <<param>>.bottom_height
  expr: Constraints[18] = <<param>>.terminal_thickness
  sketch-geometry (15):
    g0: LineSegment StartX=10.25 StartY=-12.9 StartZ=0 EndX=11.25 EndY=-12.9 EndZ=0
    g1: LineSegment StartX=11.25 StartY=-12.9 StartZ=0 EndX=11.25 EndY=-19.5 EndZ=0
    g2: LineSegment StartX=11.25 StartY=-19.5 StartZ=0 EndX=10.25 EndY=-19.5 EndZ=0
    g3: LineSegment StartX=10.25 StartY=-19.5 StartZ=0 EndX=10.25 EndY=-12.9 EndZ=0
    g4: LineSegment StartX=-10.25 StartY=-12.9 StartZ=0 EndX=-11.25 EndY=-12.9 EndZ=0
    g5: LineSegment StartX=-11.25 StartY=-12.9 StartZ=0 EndX=-11.25 EndY=-19.5 EndZ=0
    g6: LineSegment StartX=-11.25 StartY=-19.5 StartZ=0 EndX=-10.25 EndY=-19.5 EndZ=0
    g7: LineSegment StartX=-10.25 StartY=-19.5 StartZ=0 EndX=-10.25 EndY=-12.9 EndZ=0
    g8: Circle CenterX=0 CenterY=-24 CenterZ=0 NormalX=0 NormalY=0 NormalZ=1 AngleXU=0 Radius=3
    g9: LineSegment StartX=4.5 StartY=-24 StartZ=0 EndX=11.5 EndY=-24 EndZ=0
    g10: LineSegment StartX=11.5 StartY=-24 StartZ=0 EndX=11.5 EndY=-22.8 EndZ=0
    g11: LineSegment StartX=10.5 StartY=-21.8 StartZ=0 EndX=5.5 EndY=-21.8 EndZ=0
    g12: LineSegment StartX=4.5 StartY=-22.8 StartZ=0 EndX=4.5 EndY=-24 EndZ=0
    g13: ArcOfCircle CenterX=5.5 CenterY=-22.8 CenterZ=0 NormalX=0 NormalY=0 NormalZ=1 AngleXU=0 Radius=1 StartAngle=1.5708 EndAngle=3.14159
    g14: ArcOfCircle CenterX=10.5 CenterY=-22.8 CenterZ=0 NormalX=0 NormalY=0 NormalZ=1 AngleXU=0 Radius=1 StartAngle=7e-16 EndAngle=1.5708
  constraints (42):
    c: Coincident(g0,g1)
    c: Coincident(g1,g2)
    c: Coincident(g2,g3)
    c: Coincident(g3,g0)
    c: Horizontal(g0)
    c: Horizontal(g2)
    c: Vertical(g1)
    c: Vertical(g3)
    c: Coincident(g4,g5)
    c: Coincident(g5,g6)
    c: Coincident(g6,g7)
    c: Coincident(g7,g4)
    c: Horizontal(g4)
    c: Horizontal(g6)
    c: Vertical(g5)
    c: Vertical(g7)
    c: Equal(g7,g1)
    c: Equal(g4,g0)
    c: DistanceX(g4,g4) = 1
    c: DistanceY(g3,g3) = 6.6
    c: PointOnObject(g8,g-2)
    c: Radius(g8) = 3
    c: DistanceY(g8,g-1) = 24
    c: DistanceY(g8,g1) = 4.5
    c: DistanceX(g6,g1) = 21.5
    c: Symmetric(g4,g0,g-2)
    c: Coincident(g9,g10)
    c: Coincident(g12,g9)
    c: Horizontal(g9)
    c: Horizontal(g11)
    c: Vertical(g10)
    c: Vertical(g12)
    c: Tangent(g12,g13) = -1.5708
    c: Tangent(g11,g13) = -1.5708
    c: Tangent(g11,g14) = -1.5708
    c: Tangent(g10,g14) = -1.5708
    c: DistanceX(g9,g9) = 7
    c: DistanceY(g9,g11) = 2.2
    c: DistanceX(g8,g9) = 4.5
    c: Equal(g13,g14)
    c: Radius(g14) = 1
    c: DistanceY(g8,g9) = 0
FEATURE [Sketcher::SketchObject] Sketch029  label="SketchAccess"
  AttachmentOffset = pos=(0,0,-41) rot=(0,0,1;0rad)
  FullyConstrained = true
  MapMode = 5
  Placement = pos=(0,41,9.1e-15) rot=(1,0,0;1.5708rad)
  Support = -> [XZ_Plane004]
  expr: .AttachmentOffset.Base.z = -<<param>>.mid_depth / 2
  expr: Constraints[5] = <<param>>.bottom_height
  expr: Constraints[17] = <<param>>.terminal_seperation + <<param>>.terminal_thickness * 2
  expr: Constraints[25] = <<param>>.terminal_offset - 1
  sketch-geometry (9):
    g0: LineSegment StartX=-11.75 StartY=-0.5 StartZ=0 EndX=-11.75 EndY=-20.5 EndZ=0
    g1: LineSegment StartX=-7.95 StartY=-0.5 StartZ=0 EndX=-7.95 EndY=-20.5 EndZ=0
    g2: LineSegment StartX=7.95 StartY=-0.5 StartZ=0 EndX=7.95 EndY=-20.5 EndZ=0
    g3: LineSegment StartX=11.75 StartY=-0.5 StartZ=0 EndX=11.75 EndY=-20.5 EndZ=0
    g4: Circle CenterX=0 CenterY=-24 CenterZ=0 NormalX=0 NormalY=0 NormalZ=1 AngleXU=0 Radius=3
    g5: LineSegment StartX=-11.75 StartY=-20.5 StartZ=0 EndX=-7.95 EndY=-20.5 EndZ=0
    g6: LineSegment StartX=-11.75 StartY=-0.5 StartZ=0 EndX=-7.95 EndY=-0.5 EndZ=0
    g7: LineSegment StartX=7.95 StartY=-0.5 StartZ=0 EndX=11.75 EndY=-0.5 EndZ=0
    g8: LineSegment StartX=7.95 StartY=-20.5 StartZ=0 EndX=11.75 EndY=-20.5 EndZ=0
  constraints (26):
    c: Vertical(g0)
    c: Vertical(g2)
    c: Equal(g1,g2)
    c: PointOnObject(g4,g-2)
    c: Radius(g4) = 3
    c: DistanceY(g4,g-1) = 24
    c: Coincident(g5,g0)
    c: Coincident(g5,g1)
    c: Coincident(g6,g0)
    c: Coincident(g6,g1)
    c: Horizontal(g6)
    c: Coincident(g7,g2)
    c: Coincident(g7,g3)
    c: Horizontal(g7)
    c: Coincident(g8,g2)
    c: Coincident(g8,g3)
    c: Horizontal(g8)
    c: DistanceX(g0,g3) = 23.5
    c: Vertical(g3)
    c: Equal(g7,g6)
    c: DistanceY(g3,g3) = 20
    c: Symmetric(g1,g2,g-2)
    c: DistanceX(g6,g6) = 3.8
    c: Vertical(g1)
    c: Horizontal(g5)
    c: DistanceY(g4,g1) = 3.5
FEATURE [PartDesign::Pad] Pad  label="PadSide"
  Direction = (1,1,1)
  Length = 110
  Length2 = 100
  Midplane = true
  Placement = pos=(0,0,0) rot=(0.57735,0.57735,0.57735;2.0944rad)
  Profile = -> Sketch012
  Type = 0
FEATURE [Sketcher::SketchObject] Sketch030  label="SketchFront"
  AttachmentOffset = pos=(0,0,41) rot=(0,0,1;0rad)
  FullyConstrained = true
  MapMode = 5
  Placement = pos=(0,-41,-9.1e-15) rot=(1,0,0;1.5708rad)
  Support = -> [XZ_Plane004]
  expr: .AttachmentOffset.Base.z = <<param>>.mid_depth / 2
  expr: Constraints[13] = <<param>>.front_width2
  expr: Constraints[12] = <<param>>.bottom_height
  expr: Constraints[15] = <<param>>.front_height + 14
  expr: Constraints[29] = <<param>>.radius_big
  expr: Constraints[14] = <<param>>.front_width2
  expr: Constraints[9] = <<param>>.radius_small
  expr: Constraints[10] = <<param>>.bottom_width
  sketch-geometry (16):
    g0: LineSegment StartX=-47 StartY=53 StartZ=0 EndX=47 EndY=53 EndZ=0
    g1: LineSegment StartX=47 StartY=53 StartZ=0 EndX=47 EndY=5.97913 EndZ=0
    g2: LineSegment StartX=36 StartY=-5.97912 StartZ=0 EndX=36 EndY=-22 EndZ=0
    g3: LineSegment StartX=34 StartY=-24 StartZ=0 EndX=-34 EndY=-24 EndZ=0
    g4: LineSegment StartX=-36 StartY=-22 StartZ=0 EndX=-36 EndY=-5.97912 EndZ=0
    g5: LineSegment StartX=-47 StartY=5.97912 StartZ=0 EndX=-47 EndY=53 EndZ=0
    g6: ArcOfCircle CenterX=-34 CenterY=-22 CenterZ=0 NormalX=0 NormalY=0 NormalZ=1 AngleXU=0 Radius=2 StartAngle=3.14159 EndAngle=4.71239
    g7: ArcOfCircle CenterX=34 CenterY=-22 CenterZ=0 NormalX=0 NormalY=0 NormalZ=1 AngleXU=0 Radius=2 StartAngle=4.71239 EndAngle=6.28319
    g8: LineSegment StartX=-75 StartY=75 StartZ=0 EndX=75 EndY=75 EndZ=0
    g9: LineSegment StartX=75 StartY=75 StartZ=0 EndX=75 EndY=-75 EndZ=0
    g10: LineSegment StartX=75 StartY=-75 StartZ=0 EndX=-75 EndY=-75 EndZ=0
    g11: LineSegment StartX=-75 StartY=-75 StartZ=0 EndX=-75 EndY=75 EndZ=0
    g12: ArcOfCircle CenterX=42 CenterY=-5.97912 CenterZ=0 NormalX=0 NormalY=0 NormalZ=1 AngleXU=0 Radius=5.99999 StartAngle=1.65423 EndAngle=3.14159
    g13: ArcOfCircle CenterX=41 CenterY=5.97913 CenterZ=0 NormalX=0 NormalY=0 NormalZ=1 AngleXU=0 Radius=6 StartAngle=4.79582 EndAngle=6.28319
    g14: ArcOfCircle CenterX=-42 CenterY=-5.97912 CenterZ=0 NormalX=0 NormalY=0 NormalZ=1 AngleXU=0 Radius=5.99999 StartAngle=6.28319 EndAngle=7.77055
    g15: ArcOfCircle CenterX=-41 CenterY=5.97913 CenterZ=0 NormalX=0 NormalY=0 NormalZ=1 AngleXU=0 Radius=6 StartAngle=3.14159 EndAngle=4.62896
  constraints (42):
    c: Coincident(g0,g1)
    c: Vertical(g2)
    c: Vertical(g4)
    c: Coincident(g5,g0)
    c: Tangent(g4,g6) = 1.5708
    c: Tangent(g3,g6) = 1.5708
    c: Tangent(g3,g7) = 1.5708
    c: Tangent(g2,g7) = 1.5708
    c: Equal(g7,g6)
    c: Radius(g7) = 2
    c: DistanceX(g4,g2) = 72
    c: Symmetric(g3,g3,g-2)
    c: DistanceY(g3,g-1) = 24
    c: DistanceX(g5,g1) = 94
    c: DistanceX(g0,g0) = 94
    c: DistanceY(g3,g0) = 77
    c: Symmetric(g0,g0,g-2)
    c: Coincident(g8,g9)
    c: Coincident(g9,g10)
    c: Coincident(g10,g11)
    c: Coincident(g11,g8)
    c: Horizontal(g10)
    c: Vertical(g11)
    c: Symmetric(g8,g8,g-2)
    c: Symmetric(g8,g9,g-1)
    c: Equal(g8,g9)
    c: Coincident(g14,g4)
    c: Coincident(g15,g14)
    c: Coincident(g15,g5)
    c: Radius(g13) = 6
    c: DistanceX(g8,g8) = 150
    c: Vertical(g5)
    c: Tangent(g13,g12) = 1.5708
    c: Tangent(g13,g1) = 1.5708
    c: Tangent(g12,g2) = -1.5708
    c: Tangent(g14,g4)
    c: Tangent(g14,g15)
    c: Symmetric(g5,g4,g14)
    c: Equal(g14,g12)
    c: Equal(g13,g15)
    c: PointOnObject(g12,g-1)
    c: PointOnObject(g14,g-1)
FEATURE [Sketcher::SketchObject] Sketch031  label="SketchRear"
  AttachmentOffset = pos=(0,0,-41) rot=(0,0,1;0rad)
  FullyConstrained = true
  MapMode = 5
  Placement = pos=(0,41,9.1e-15) rot=(1,0,0;1.5708rad)
  Support = -> [XZ_Plane004]
  expr: Constraints[16] = <<param>>.rear_width
  expr: .AttachmentOffset.Base.z = -<<param>>.mid_depth / 2
  expr: Constraints[4] = <<param>>.front_height + 14
  expr: Constraints[1] = <<param>>.radius_small
  expr: Constraints[5] = <<param>>.bottom_height
  expr: Constraints[2] = <<param>>.rear_width
  sketch-geometry (10):
    g0: LineSegment StartX=-34 StartY=-24 StartZ=0 EndX=34 EndY=-24 EndZ=0
    g1: LineSegment StartX=36 StartY=53 StartZ=0 EndX=-36 EndY=53 EndZ=0
    g2: ArcOfCircle CenterX=-34 CenterY=-22 CenterZ=0 NormalX=0 NormalY=0 NormalZ=1 AngleXU=0 Radius=2 StartAngle=3.14159 EndAngle=4.71239
    g3: ArcOfCircle CenterX=34 CenterY=-22 CenterZ=0 NormalX=0 NormalY=0 NormalZ=1 AngleXU=0 Radius=2 StartAngle=4.71238 EndAngle=6.28319
    g4: LineSegment StartX=-75 StartY=75 StartZ=0 EndX=75 EndY=75 EndZ=0
    g5: LineSegment StartX=75 StartY=75 StartZ=0 EndX=75 EndY=-75 EndZ=0
    g6: LineSegment StartX=75 StartY=-75 StartZ=0 EndX=-75 EndY=-75 EndZ=0
    g7: LineSegment StartX=-75 StartY=-75 StartZ=0 EndX=-75 EndY=75 EndZ=0
    g8: LineSegment StartX=36 StartY=-22 StartZ=0 EndX=36 EndY=53 EndZ=0
    g9: LineSegment StartX=-36 StartY=-22 StartZ=0 EndX=-36 EndY=53 EndZ=0
  constraints (29):
    c: Horizontal(g0)
    c: Radius(g3) = 2
    c: DistanceX(g1,g1) = 72
    c: Symmetric(g1,g1,g-2)
    c: DistanceY(g0,g1) = 77
    c: DistanceY(g0,g-1) = 24
    c: Coincident(g4,g5)
    c: Coincident(g5,g6)
    c: Coincident(g6,g7)
    c: Coincident(g7,g4)
    c: Horizontal(g4)
    c: Vertical(g7)
    c: Symmetric(g5,g6,g-2)
    c: DistanceX(g4,g4) = 150
    c: Equal(g4,g5)
    c: Symmetric(g4,g5,g-1)
    c: DistanceX(g2,g3) = 72
    c: Coincident(g8,g3)
    c: Coincident(g8,g1)
    c: Vertical(g8)
    c: Coincident(g9,g2)
    c: Coincident(g9,g1)
    c: Equal(g9,g8)
    c: Horizontal(g3,g3)
    c: Horizontal(g2,g2)
    c: Equal(g2,g3)
    c: Coincident(g0,g2)
    c: Coincident(g0,g3)
    c: Vertical(g2,g0)
FEATURE [PartDesign::SubtractiveLoft] SubtractiveLoft001  label="SubtractiveLoftTaper"
  BaseFeature = -> Pad
  Closed = false
  Placement = pos=(0,0,0) rot=(0.57735,0.57735,0.57735;2.0944rad)
  Profile = -> Sketch031
  Ruled = true
  Sections = -> [Sketch030]
FEATURE [PartDesign::Pocket] Pocket  label="PocketBatt"
  BaseFeature = -> SubtractiveLoft001
  Length = 14.6
  Length2 = 100
  Placement = pos=(0,0,0) rot=(0.57735,0.57735,0.57735;2.0944rad)
  Profile = -> Sketch018
  Reversed = true
  Type = 0
  expr: Length = Spreadsheet.batt_carveout
FEATURE [PartDesign::Pad] Pad004  label="PadRail"
  BaseFeature = -> Pocket
  Direction = (1,1,1)
  Length = 45
  Length2 = 100
  Placement = pos=(0,0,0) rot=(0.57735,0.57735,0.57735;2.0944rad)
  Profile = -> Sketch019
  Type = 0
  expr: Length = <<param>>.batt_rail_length
FEATURE [PartDesign::Pocket] Pocket002  label="PocketRear"
  BaseFeature = -> Pad004
  Length = 6
  Length2 = 100
  Placement = pos=(0,0,0) rot=(0.57735,0.57735,0.57735;2.0944rad)
  Profile = -> Sketch
  Type = 0
FEATURE [PartDesign::SubtractiveLoft] SubtractiveLoft  label="SubtractiveLoftInside"
  BaseFeature = -> Pocket002
  Closed = false
  Placement = pos=(0,0,0) rot=(0.57735,0.57735,0.57735;2.0944rad)
  Profile = -> Sketch022
  Ruled = true
  Sections = -> [Sketch025,Sketch023]
FEATURE [PartDesign::Pocket] Pocket003  label="PocketFace"
  BaseFeature = -> SubtractiveLoft
  Length = 3.2
  Length2 = 100
  Placement = pos=(0,0,0) rot=(0.57735,0.57735,0.57735;2.0944rad)
  Profile = -> Sketch024
  Reversed = true
  Type = 0
  expr: Length = <<param>>.face_thickness + 0.2
FEATURE [PartDesign::Pocket] Pocket004  label="PocketFrontScrews"
  BaseFeature = -> Pocket003
  Length = 6
  Length2 = 100
  Placement = pos=(0,0,0) rot=(0.57735,0.57735,0.57735;2.0944rad)
  Profile = -> Sketch026
  Type = 0
FEATURE [PartDesign::Revolution] Revolution  label="RevolutionButton"
  Angle = 360
  Axis = (-1e-16,0.292372,0.956305)
  Base = (-2.9e-15,10,23)
  BaseFeature = -> Pocket004
  Placement = pos=(0,0,0) rot=(0.57735,0.57735,0.57735;2.0944rad)
  Profile = -> Sketch021
  ReferenceAxis = -> Sketch021 [V_Axis]
  Reversed = true
FEATURE [PartDesign::Pocket] Pocket005  label="PocketButtonHole"
  BaseFeature = -> Revolution
  Length = 6
  Length2 = 100
  Placement = pos=(0,0,0) rot=(0.57735,0.57735,0.57735;2.0944rad)
  Profile = -> Sketch008
  Reversed = true
  Type = 1
FEATURE [PartDesign::Groove] Groove  label="GrooveButton"
  Angle = 360
  Axis = (-1e-16,0.292372,0.956305)
  Base = (-2.9e-15,10,23)
  BaseFeature = -> Pocket005
  Placement = pos=(0,0,0) rot=(0.57735,0.57735,0.57735;2.0944rad)
  Profile = -> Sketch027
  ReferenceAxis = -> Sketch027 [V_Axis]
FEATURE [PartDesign::Pocket] Pocket007  label="PocketTerminals"
  BaseFeature = -> Groove
  Length = 5
  Length2 = 100
  Midplane = true
  Placement = pos=(0,0,0) rot=(0.57735,0.57735,0.57735;2.0944rad)
  Profile = -> Sketch028
  Type = 1
FEATURE [PartDesign::Pocket] Pocket008  label="PocketAccess"
  BaseFeature = -> Pocket007
  Length = 22
  Length2 = 100
  Placement = pos=(0,0,0) rot=(0.57735,0.57735,0.57735;2.0944rad)
  Profile = -> Sketch029
  Reversed = true
  Type = 0
  expr: Length = <<param>>.terminal_depth
FEATURE [Sketcher::SketchObject] Sketch032  label="SketchBack"
  FullyConstrained = true
  MapMode = 5
  Placement = pos=(0,0,0) rot=(1,0,0;1.5708rad)
  Support = -> [XZ_Plane005]
  expr: Constraints[27] = <<param>>.reart_screw_width2
  expr: Constraints[17] = <<param>>.rear_height
  expr: Constraints[14] = <<param>>.bottom_height
  expr: Constraints[31] = <<param>>.rear_screw_offset
  expr: Constraints[28] = <<param>>.rear_screw_height
  expr: Constraints[25] = <<param>>.screw_hole + 1
  expr: Constraints[18] = <<param>>.rear_width
  expr: Constraints[16] = <<param>>.radius_small
  expr: Constraints[15] = <<param>>.radius_big
  expr: Constraints[26] = <<param>>.rear_screw_width1
  sketch-geometry (13):
    g0: LineSegment StartX=-30 StartY=17 StartZ=0 EndX=30 EndY=17 EndZ=0
    g1: LineSegment StartX=36 StartY=11 StartZ=0 EndX=36 EndY=-22 EndZ=0
    g2: LineSegment StartX=34 StartY=-24 StartZ=0 EndX=-34 EndY=-24 EndZ=0
    g3: LineSegment StartX=-36 StartY=-22 StartZ=0 EndX=-36 EndY=11 EndZ=0
    g4: ArcOfCircle CenterX=-30 CenterY=11 CenterZ=0 NormalX=0 NormalY=0 NormalZ=1 AngleXU=0 Radius=6 StartAngle=1.5708 EndAngle=3.14159
    g5: ArcOfCircle CenterX=30 CenterY=11 CenterZ=0 NormalX=0 NormalY=0 NormalZ=1 AngleXU=0 Radius=6 StartAngle=0 EndAngle=1.5708
    g6: ArcOfCircle CenterX=34 CenterY=-22 CenterZ=0 NormalX=0 NormalY=0 NormalZ=1 AngleXU=0 Radius=2 StartAngle=4.71239 EndAngle=6.28319
    g7: ArcOfCircle CenterX=-34 CenterY=-22 CenterZ=0 NormalX=0 NormalY=0 NormalZ=1 AngleXU=0 Radius=2 StartAngle=3.14159 EndAngle=4.71239
    g8: Circle CenterX=-29 CenterY=8.9 CenterZ=0 NormalX=0 NormalY=0 NormalZ=1 AngleXU=0 Radius=1.75
    g9: Circle CenterX=0 CenterY=8.9 CenterZ=0 NormalX=0 NormalY=0 NormalZ=1 AngleXU=0 Radius=1.75
    g10: Circle CenterX=29 CenterY=8.9 CenterZ=0 NormalX=0 NormalY=0 NormalZ=1 AngleXU=0 Radius=1.75
    g11: Circle CenterX=-27.5 CenterY=-16.6 CenterZ=0 NormalX=0 NormalY=0 NormalZ=1 AngleXU=0 Radius=1.75
    g12: Circle CenterX=27.5 CenterY=-16.6 CenterZ=0 NormalX=0 NormalY=0 NormalZ=1 AngleXU=0 Radius=1.75
  constraints (32):
    c: Horizontal(g0)
    c: Vertical(g1)
    c: Vertical(g3)
    c: Tangent(g3,g4) = 1.5708
    c: Tangent(g0,g4) = 1.5708
    c: Tangent(g0,g5) = 1.5708
    c: Tangent(g1,g5) = 1.5708
    c: Tangent(g2,g6) = 1.5708
    c: Tangent(g1,g6) = 1.5708
    c: Tangent(g3,g7) = 1.5708
    c: Tangent(g2,g7) = 1.5708
    c: Equal(g6,g7)
    c: Equal(g5,g4)
    c: Symmetric(g2,g2,g-2)
    c: DistanceY(g2,g-1) = 24
    c: Radius(g4) = 6
    c: Radius(g7) = 2
    c: DistanceY(g2,g0) = 41
    c: DistanceX(g3,g1) = 72
    c: Symmetric(g8,g10,g-2)
    c: Symmetric(g11,g12,g-2)
    c: Equal(g11,g8)
    c: Equal(g8,g9)
    c: Equal(g9,g10)
    c: Equal(g10,g12)
    c: Diameter(g8) = 3.5
    c: DistanceX(g8,g10) = 58
    c: DistanceX(g11,g12) = 55
    c: DistanceY(g12,g10) = 25.5
    c: Horizontal(g8,g9)
    c: PointOnObject(g9,g-2)
    c: DistanceY(g2,g12) = 7.4
FEATURE [PartDesign::Pad] Pad005  label="PadBack"
  Direction = (1,1,1)
  Length = 5
  Length2 = 100
  Placement = pos=(0,0,0) rot=(1,0,0;1.5708rad)
  Profile = -> Sketch032
  Type = 0
FEATURE [PartDesign::Chamfer] Chamfer  label="ChamferBack"
  Angle = 45
  Base = -> Pad005 [Edge26,Edge38,Edge35,Edge32,Edge29]
  BaseFeature = -> Pad005
  ChamferType = 0
  FlipDirection = false
  Placement = pos=(0,0,0) rot=(1,0,0;1.5708rad)
  Size = 1.4
  Size2 = 1
  SupportTransform = false
FEATURE [PartDesign::Fillet] Fillet002  label="FilletBack"
  Base = -> Chamfer [Edge22,Edge21,Edge20,Edge19,Edge18,Edge25,Edge24,Edge23]
  BaseFeature = -> Chamfer
  Placement = pos=(0,0,0) rot=(1,0,0;1.5708rad)
  Radius = 4.4
  SupportTransform = false
FEATURE [PartDesign::Body] Body  label="BodyBack"
  Group = -> [Sketch032,Pad005,Chamfer,Fillet002]
  Origin = -> Origin005
  Placement = pos=(0,46,0) rot=(0,0,1;0rad)
  Tip = -> Fillet002
  expr: .Placement.Base.y = <<param>>.mid_depth / 2 + 5
FEATURE [Mesh::Feature] Mesh001  label="BodyBack (Meshed)"
FEATURE [PartDesign::Fillet] Fillet
  Base = -> Pocket008 [Edge197,Edge196]
  BaseFeature = -> Pocket008
  Placement = pos=(0,0,0) rot=(0.57735,0.57735,0.57735;2.0944rad)
  Radius = 6
  SupportTransform = false
  expr: Radius = <<param>>.radius_big
FEATURE [PartDesign::Body] Body003  label="Body"
  Group = -> [Pad,SubtractiveLoft001,Sketch031,Sketch030,Sketch018,Pocket,Sketch019,Pad004,Pocket002,Sketch008,Sketch021,Sketch022,Sketch025,Sketch023,Sketch024,Sketch,SubtractiveLoft,Pocket003,Sketch026,Pocket004,Revolution,Pocket005,Groove,Sketch027,Sketch028,Pocket007,Sketch029,Pocket008,Sketch012,Fillet]
  Origin = -> Origin004
  Tip = -> Fillet
FEATURE [App::Part] Part
  Group = -> [Body003,Body]
  Origin = -> Origin
FEATURE [Part::Fillet] Fillet003  label="FilletFinal"
  Base = -> Fillet
  Edges = 5 edges r=1.9: [Edge1,Edge4,Edge8,Edge27,Edge37]
FEATURE [Mesh::Feature] Mesh  label="FilletFinal (Meshed)"
FEATURE [App::DocumentObjectGroup] Group  label="Mesh"
  Group = -> [Mesh001,Mesh]
